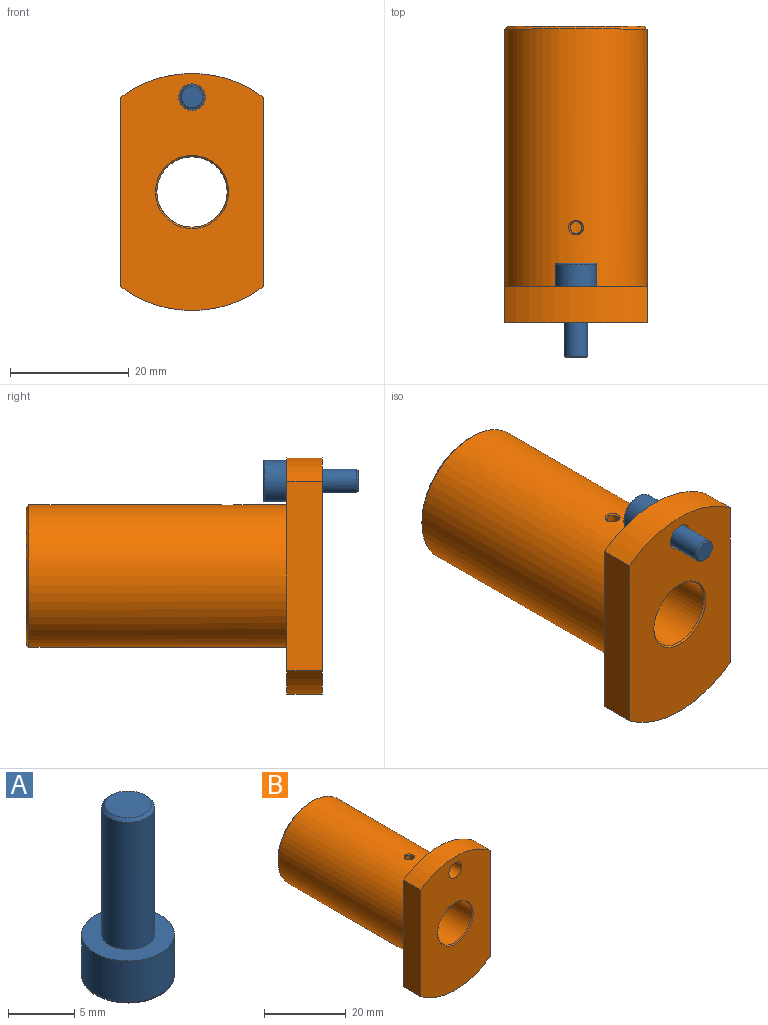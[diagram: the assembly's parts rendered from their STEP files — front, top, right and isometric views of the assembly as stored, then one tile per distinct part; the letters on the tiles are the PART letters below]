
ASSEMBLY  parts=2 mates=1
PART A: 14 faces, bbox 7.6x7.6x16 mm
  f0: plane 7x7mm, normal (0,0,1), area 25.9mm2, adj f1,f3,f6,f7,f8,f9,f10,f11
  f1: cylinder r=3.5mm len=7mm, axis (0,0,-1), area 82.5mm2, adj f0,f12
  f2: plane 6.5x6.5mm, normal (0,0,-1), area 22.6mm2, adj f6,f7,f8,f9,f10,f11,f12
  f3: cylinder r=2mm len=11.75mm, axis (0,0,-1), area 147.7mm2, adj f0,f5,f13
  f4: plane 3.5x3.5mm, normal (0,0,1), area 9.6mm2, adj f13
  f5: plane 4x3.5mm, normal (0,0,-1), area 10.6mm2, adj f3,f6,f7,f8,f9,f10,f11
  f6: plane 4x1.75mm, normal (0.87,-0.5,0), area 8.1mm2, adj f0,f2,f5,f7,f11
  f7: plane 4x1.75mm, normal (0.87,0.5,0), area 8.1mm2, adj f0,f2,f5,f6,f8
  f8: plane 4x2.02mm, normal (0,1,0), area 8.1mm2, adj f0,f2,f5,f7,f9
  f9: plane 4x1.75mm, normal (-0.87,0.5,0), area 8.1mm2, adj f0,f2,f5,f8,f10
  f10: plane 4x1.75mm, normal (-0.87,-0.5,0), area 8.1mm2, adj f0,f2,f5,f9,f11
  f11: plane 4x2.02mm, normal (0,-1,0), area 8.1mm2, adj f0,f2,f5,f6,f10
  f12: torus R=3.25mm, axis (0,0,1), area 8.4mm2, adj f1,f2
  f13: cone r=1.75mm half-angle=45deg, axis (0,0,-1), area 4.2mm2, adj f3,f4
PART B: 16 faces, bbox 24x50x40 mm
  f0: cylinder r=12mm len=43.5mm, axis (0,-1,0), area 3275mm2, adj f4,f5,f13,f15
  f1: cylinder r=5.92mm len=49.5mm, axis (0,-1,0), area 1839.6mm2, adj f11,f12,f14
  f2: cylinder r=20mm len=24mm, axis (0,-1,0), area 154.4mm2, adj f4,f6,f9,f10
  f3: cylinder r=20mm len=24mm, axis (0,-1,0), area 154.4mm2, adj f5,f6,f9,f10
  f4: plane 24x20mm, normal (0,1,0), area 207.3mm2, adj f0,f2,f8,f9,f10
  f5: plane 24x20mm, normal (0,1,0), area 223.2mm2, adj f0,f3,f9,f10
  f6: plane 40x24mm, normal (0,-1,0), area 763.1mm2, adj f2,f3,f8,f9,f10,f11
  f7: plane 23x23mm, normal (0,1,0), area 295.7mm2, adj f12,f13
  f8: cylinder r=2.25mm len=6mm, axis (0,-1,0), area 84.8mm2, adj f4,f6
  f9: plane 32x6mm, normal (1,0,0), area 192mm2, adj f2,f3,f4,f5,f6
  f10: plane 32x6mm, normal (-1,0,0), area 192mm2, adj f2,f3,f4,f5,f6
  f11: cone r=5.92mm half-angle=45deg, axis (0,-1,0), area 13.4mm2, adj f1,f6
  f12: cone r=5.92mm half-angle=45deg, axis (0,1,0), area 13.4mm2, adj f1,f7
  f13: cone r=11.5mm half-angle=45deg, axis (0,-1,0), area 52.2mm2, adj f0,f7
  f14: cylinder r=1mm len=5.87mm, axis (0,0,1), area 36.9mm2, adj f1,f15
  f15: bspline ~2.51x2.46mm, area 2.3mm2, adj f0,f14
PLACE A rot(axis=(1,0,0),90deg) t=(0.57,30.94,1.22)mm
PLACE B at identity
MATE fastened A.f1 <-> B.f8  axis (0,-1,0) through (0,6,16)mm
